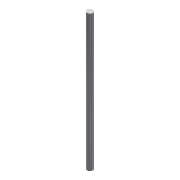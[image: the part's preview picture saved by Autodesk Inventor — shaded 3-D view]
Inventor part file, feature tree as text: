
AUTODESK INVENTOR PART (.ipt)
format: ipt  version: 2015 (Build 190159000, 159)  size: 96,768 bytes
history: native  units: mm
features: hole x2, extrude x1, sketch x1
ambient origin geometry x8: Origin, YZ Plane, XZ Plane, XY Plane, X Axis, Y Axis, Z Axis, Center Point
bodies: Solid1 (feature_tree)
feature tree (4):
  extrude  "Extrusion1"  Depth=440.0mm TaperAngle=0.0deg
  hole  "Hole1"  [1 undecoded]
  hole  "Hole2"  [1 undecoded]
  sketch  "Sketch1"  dims[d0=19.0mm d1=440.0mm d2=0.0mm d3=10.0mm d4=10.0mm d5=10.0mm d6=6.0mm d7=4.0mm d8=2.0mm d9=90.0deg d10=70.0mm d11=20.594885mm d12=10.0mm d13=10.0mm d14=10.0mm d15=6.0mm d16=4.0mm d17=2.0mm d18=90.0deg d19=70.0mm d20=20.594885mm]
note: 2 required parameter values undecoded (feature->parameter linkage not recoverable at this tier; creation-order binding heuristic only, values carry confidence <= 0.55)
